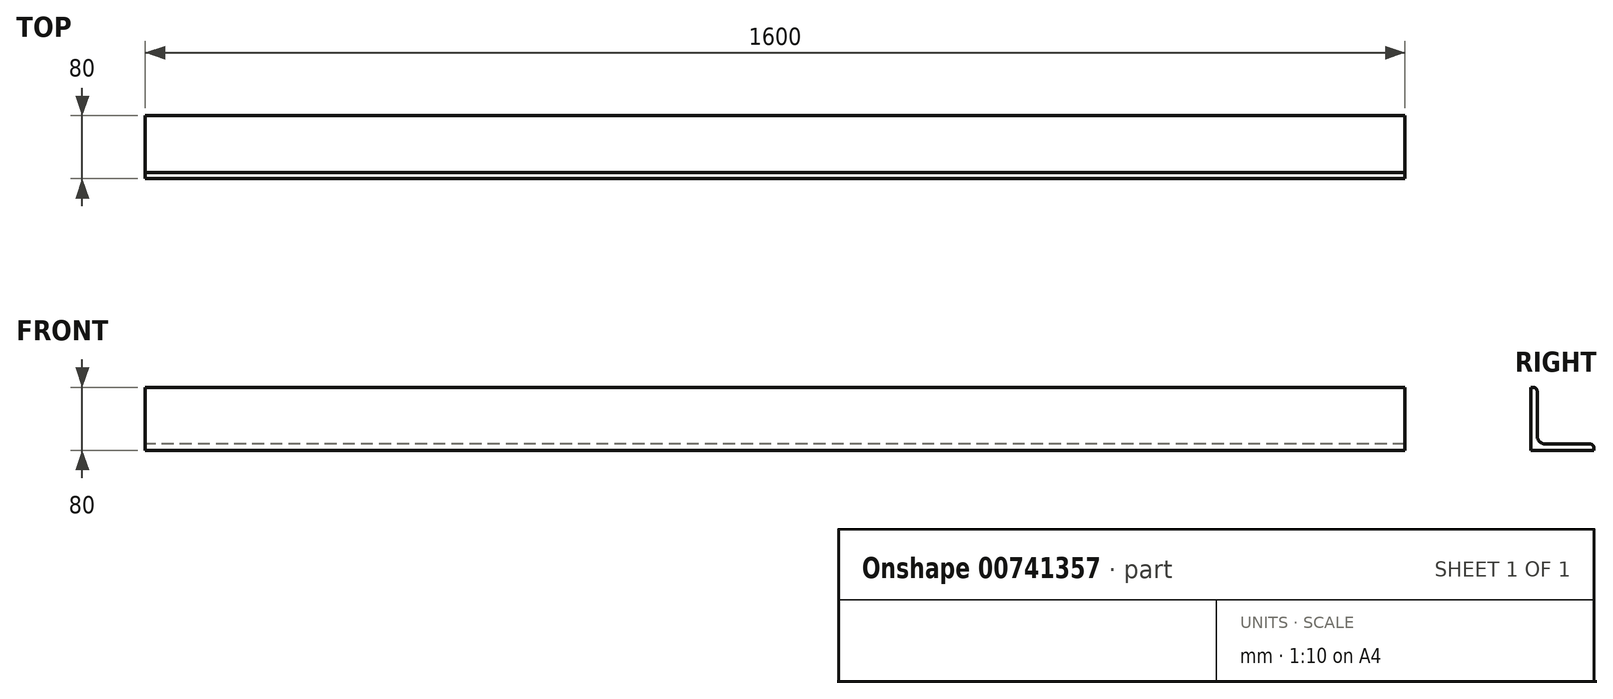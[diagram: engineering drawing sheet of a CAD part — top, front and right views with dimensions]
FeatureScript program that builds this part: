
annotation { "Feature Type Name" : "Feature", "Feature Type Description" : "" }
export const myFeature = defineFeature(function(context is Context, id is Id, definition is map)
    precondition{}
    {
        {
            var Q0;
            Q0=qCreatedBy(makeId("Right.planeOp"),FACE);
            var sketch = newSketch(context, id + "F0", { "sketchPlane" : qUnion([Q0])});
            skLineSegment(sketch, "E0", {"start": v(80, 0) * mm, "end": v(0, 0) * mm});
            skLineSegment(sketch, "E1", {"start": v(0, 0) * mm, "end": v(0, 80) * mm});
            skLineSegment(sketch, "E2", {"start": v(80, 0) * mm, "end": v(80, 3) * mm});
            skLineSegment(sketch, "E3", {"start": v(75, 8) * mm, "end": v(18, 8) * mm});
            skLineSegment(sketch, "E4", {"start": v(8, 18) * mm, "end": v(8, 75) * mm});
            skLineSegment(sketch, "E5", {"start": v(3, 80) * mm, "end": v(0, 80) * mm});
            skPoint(sketch, "E6.visualSharp", {"position": v(8, 80) * mm});
            skArc(sketch, "E6.filletArc", {"start": v(8, 75) * mm, "mid": v(6.54, 78.54) * mm, "end": v(3, 80) * mm});
            skPoint(sketch, "E7.visualSharp", {"position": v(80, 8) * mm});
            skArc(sketch, "E7.filletArc", {"start": v(80, 3) * mm, "mid": v(78.54, 6.54) * mm, "end": v(75, 8) * mm});
            skPoint(sketch, "E8.visualSharp", {"position": v(8, 8) * mm});
            skArc(sketch, "E8.filletArc", {"start": v(8, 18) * mm, "mid": v(10.93, 10.93) * mm, "end": v(18, 8) * mm});
            skSolve(sketch);
        }
        {
            var Q0;
            Q0=makeQuery(id+"F0.imprint","IMPRINT",FACE,{"disambiguationData":[TD([[makeQuery(id+"F0.imprint","IMPRINT",EDGE,{"derivedFrom":sQuery(id+"F0.wireOp",EDGE,"E0")}),-1.0]])]});
            extrude(context, id + "F1", {"entities" : qUnion([Q0]), "endBound" : BoundingType.SYMMETRIC, "depth" : 1600 * mm, "offsetDistance" : 25 * mm});
        }
    });
